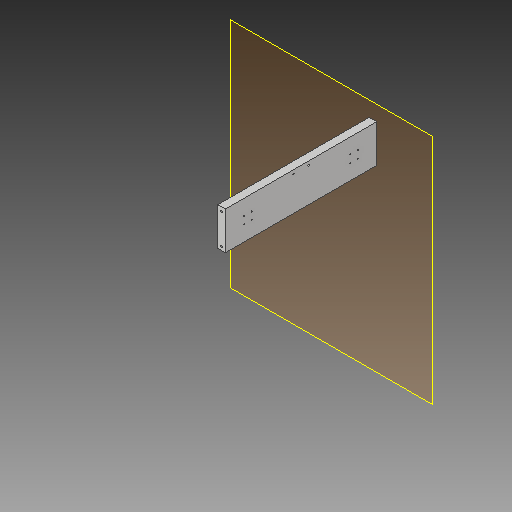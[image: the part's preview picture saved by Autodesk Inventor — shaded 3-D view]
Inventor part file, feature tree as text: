
AUTODESK INVENTOR PART (.ipt)
format: ipt  version: 2019 (Build 230136000, 136)  size: 191,488 bytes
history: native  units: in
note: dims shown in document units (in); Inventor stores cm internally (conversion verified against a paired STEP export)
features: reference x14, sketch x7, extrude x7, other x7, thread x4, plane x2, projected_geometry x1, helix x1
ambient origin geometry x8: Origin, YZ Plane, XZ Plane, XY Plane, X Axis, Y Axis, Z Axis, Center Point
bodies: Solid1 (feature_tree)
feature tree (43):
  plane  "Work Plane1"
  sketch  "Sketch1"  dims[d0=0.7874in d1=1.0in d2=0.0in]
  plane  "Work Plane2"
  extrude  "Extrusion1"  Depth=0.7874in TaperAngle=0.0deg
  extrude  "Extrusion2"  Depth=0.1181in
  extrude  "Extrusion3"  Depth=0.1181in
  extrude  "Extrusion4"  Depth=0.1181in
  extrude  "Extrusion5"  Depth=0.1181in
  extrude  "Extrusion6"  Depth=0.315in
  thread  "Thread1"  [1 undecoded]
  thread  "Thread2"  [1 undecoded]
  extrude  "Extrusion7"  Depth=0.7874in
  thread  "Thread3"  [1 undecoded]
  thread  "Thread4"  [1 undecoded]
  reference  "Reference1"
  sketch  "Sketch2"  dims[d3=0.1181in d4=0.1181in]
  reference  "Reference2"
  reference  "Reference3"
  reference  "Reference4"
  reference  "Reference5"
  reference  "Reference6"
  reference  "Reference7"
  reference  "Reference8"
  reference  "Reference9"
  sketch  "Sketch3"  dims[d5=0.1181in d6=0.1181in]
  projected_geometry  "Projected Loop1"
  sketch  "Sketch4"  dims[d7=0.1181in d8=0.1181in]
  reference  "Reference10"
  reference  "Reference11"
  sketch  "Sketch5"  dims[d9=0.1181in d10=0.1181in]
  sketch  "Sketch6"  dims[d11=1.0in d12=0.0in d13=0.315in d14=0.315in d15=0.315in]
  reference  "Reference12"
  reference  "Reference13"
  sketch  "Sketch7"  dims[d16=0.315in d17=0.315in d18=0.315in d19=0.315in d20=0.315in d21=0.1969in d22=0.0in d23=0.1575in d24=0.1575in d25=0.1969in d26=0.0in d27=0.3937in d28=0.3937in d29=0.2362in d30=0.0in d31=0.1969in d32=0.1969in d33=0.7874in d34=0.0in d35=1.0in d36=0.0in d37=1.0in d38=0.0in d39=0.1969in d40=0.1969in d41=0.7874in d42=0.0in d43=1.0in d44=0.0in d45=1.0in d46=0.0in]
  reference  "Reference14"
  other  "<userpath>\Documents\CAD Files\Helix DLP\Helix DLP Z Stage.iam"
  helix  "Helix DLP Z Stage.iam"  [1 undecoded]
  other  "Z stage_side:1"
  other  "MGN12H, LINEAR GUIDE BLOCK:1"
  other  "MGN12H, LINEAR GUIDE BLOCK:2"
  other  "Z Leadcrew Nut Holder:1"
  other  "Z stage_side:2"
  other  "Assembly1"
note: 5 required parameter values undecoded (feature->parameter linkage not recoverable at this tier; creation-order binding heuristic only, values carry confidence <= 0.55)
